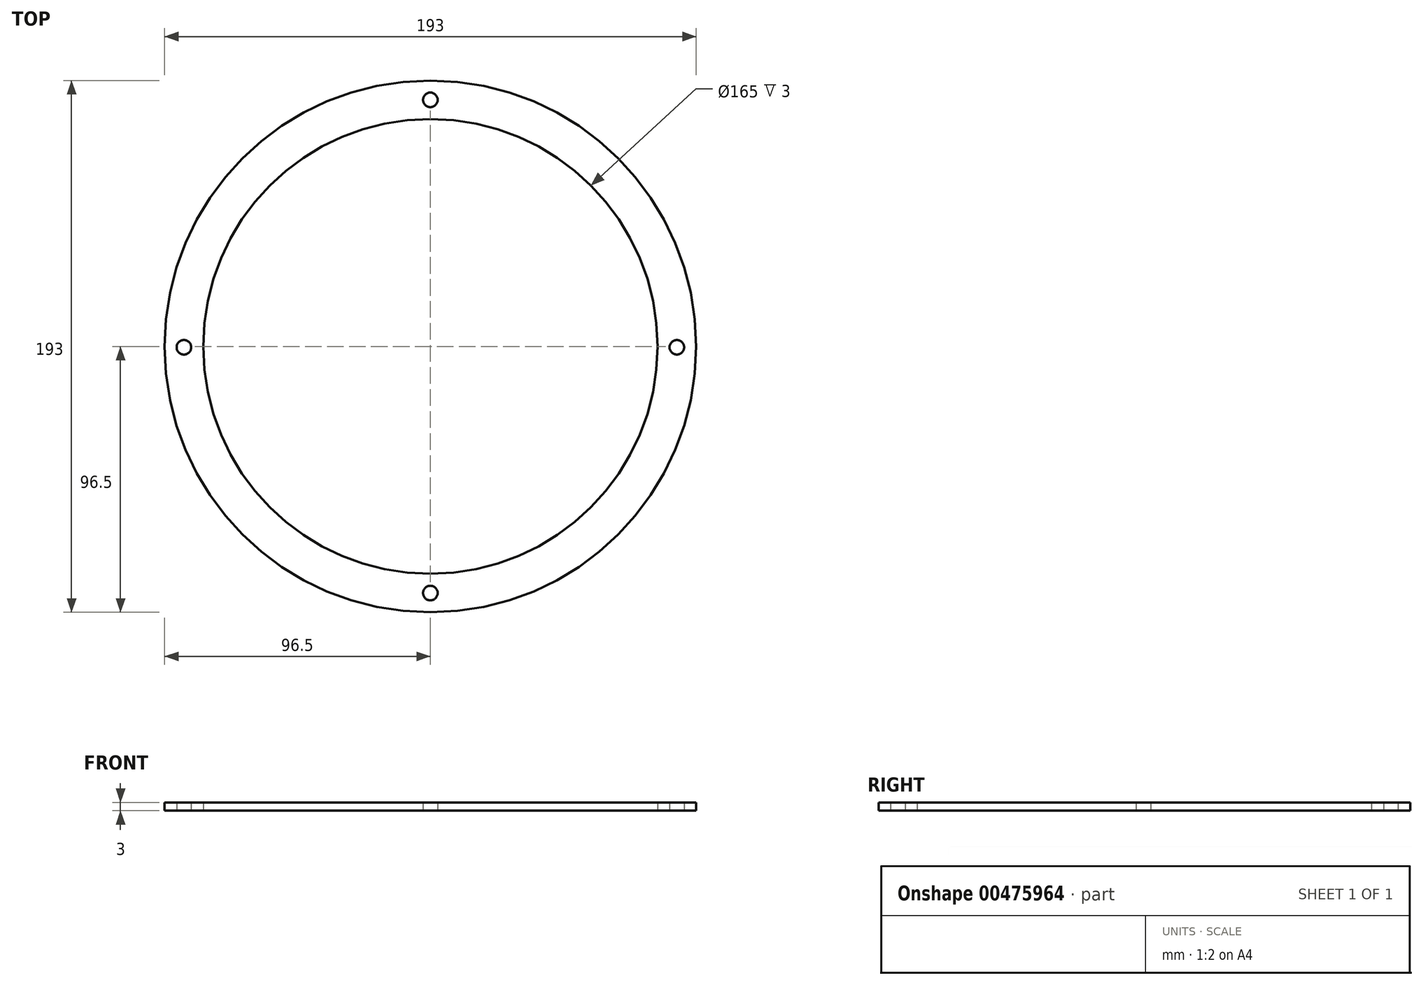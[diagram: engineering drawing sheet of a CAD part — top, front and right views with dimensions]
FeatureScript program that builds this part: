
annotation { "Feature Type Name" : "Feature", "Feature Type Description" : "" }
export const myFeature = defineFeature(function(context is Context, id is Id, definition is map)
    precondition{}
    {
        {
            var Q0;
            Q0=qCreatedBy(makeId("Top.planeOp"),FACE);
            var sketch = newSketch(context, id + "F0", { "sketchPlane" : qUnion([Q0])});
            skCircle(sketch, "E0", {"center": v(0, 0) * mm, "radius": 96.5 * mm});
            skCircle(sketch, "E1", {"center": v(0, 0) * mm, "radius": 82.5 * mm});
            skLineSegment(sketch, "E2", {"start": v(0, 0) * mm, "end": v(0, 96.5) * mm, "construction": true});
            skLineSegment(sketch, "E3", {"start": v(0, 0) * mm, "end": v(96.5, 0) * mm, "construction": true});
            skLineSegment(sketch, "E4", {"start": v(0, 0) * mm, "end": v(0, -96.5) * mm, "construction": true});
            skLineSegment(sketch, "E5", {"start": v(0, 0) * mm, "end": v(-96.5, 0) * mm, "construction": true});
            skLineSegment(sketch, "E6", {"start": v(-89.5, 11.73) * mm, "end": v(-89.5, -12.36) * mm, "construction": true});
            skCircle(sketch, "E7", {"center": v(-89.5, -0.31) * mm, "radius": 2.65 * mm});
            skCircle(sketch, "E8.MirrorC", {"center": v(89.5, -0.31) * mm, "radius": 2.65 * mm});
            skLineSegment(sketch, "E9", {"start": v(-11.24, 89.5) * mm, "end": v(14.6, 89.5) * mm, "construction": true});
            skCircle(sketch, "E10", {"center": v(0, 89.5) * mm, "radius": 2.65 * mm});
            skCircle(sketch, "E11.MirrorC", {"center": v(0, -89.5) * mm, "radius": 2.65 * mm});
            skSolve(sketch);
        }
        {
            var Q0;
            Q0=makeQuery(id+"F0.imprint","IMPRINT",FACE,{"disambiguationData":[TD([[makeQuery(id+"F0.imprint","IMPRINT",EDGE,{"derivedFrom":sQuery(id+"F0.wireOp",EDGE,"E0")}),1.0]])]});
            extrude(context, id + "F1", {"entities" : qUnion([Q0]), "depth" : 3 * mm});
        }
    });
